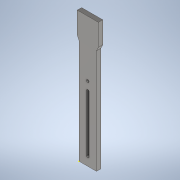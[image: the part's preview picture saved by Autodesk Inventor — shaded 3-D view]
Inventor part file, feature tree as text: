
AUTODESK INVENTOR PART (.ipt)
format: ipt  version: 2021 (Build 250183000, 183)  size: 137,216 bytes
history: native  units: mm
features: sketch x11, hole x4, extrude x2
ambient origin geometry x8: Origin, YZ Plane, XZ Plane, XY Plane, X Axis, Y Axis, Z Axis, Center Point
bodies: Solid1 (feature_tree)
feature tree (17):
  extrude  "Extrusion1"  Depth=120.0mm
  hole  "Hole1"  [1 undecoded]
  sketch  "Sketch3"  dims[d4=90.0deg d5=5.0mm]
  hole  "Hole2"  [1 undecoded]
  extrude  "Extrusion2"  Depth=5.0mm
  hole  "Hole3"  [1 undecoded]
  hole  "Hole4"  [1 undecoded]
  sketch  "Sketch10"  dims[d27=3.0mm d28=6.0mm d29=4.0mm d30=2.0mm d31=90.0deg d32=8.0mm d33=20.594885mm]
  sketch  "Sketch11"  dims[d36=3.0mm d37=6.0mm d38=4.0mm d39=2.0mm d40=90.0deg d41=8.0mm d42=20.594885mm]
  sketch  "Sketch12"  dims[d45=24.226183mm]
  sketch  "Sketch13"
  sketch  "Sketch1"  dims[d0=20.0mm d1=120.0mm]
  sketch  "Sketch2"  dims[d2=90.0deg d3=120.0mm]
  sketch  "Sketch4"  dims[d6=11.34464mm d7=5.0mm]
  sketch  "Sketch5"  dims[d8=25.0mm d9=5.0mm d10=0.0mm]
  sketch  "Sketch6"  dims[d11=3.0mm d12=6.0mm d13=4.0mm d14=2.0mm d15=90.0deg d16=8.0mm d17=20.594885mm]
  sketch  "Sketch8"  dims[d18=3.0mm d19=6.0mm d20=4.0mm d21=2.0mm d22=90.0deg d23=8.0mm d24=20.594885mm d25=10.0mm d26=0.0mm]
note: 4 required parameter values undecoded (feature->parameter linkage not recoverable at this tier; creation-order binding heuristic only, values carry confidence <= 0.55)
